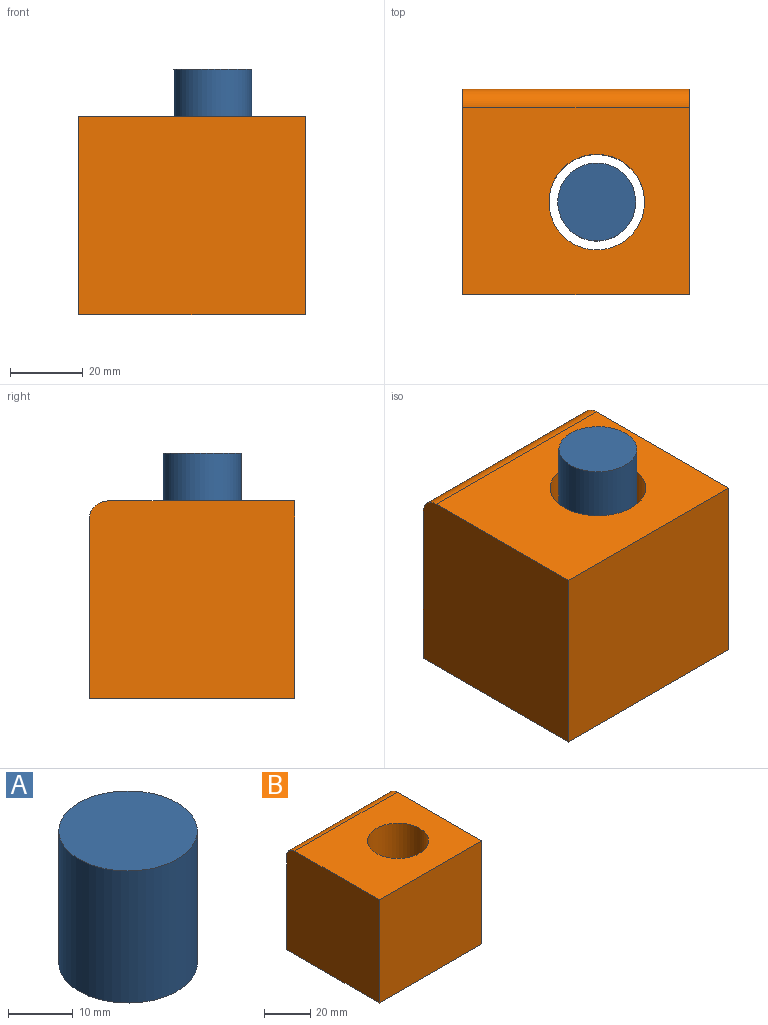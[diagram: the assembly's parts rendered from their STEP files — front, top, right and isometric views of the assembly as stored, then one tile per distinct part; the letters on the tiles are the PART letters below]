
ASSEMBLY  parts=2 mates=1
PART A: 3 faces, bbox 21.4x21.4x25 mm
  f0: cylinder r=10.71mm len=25mm, axis (0,0,-1), area 1682.9mm2, adj f1,f2
  f1: plane 21.43x21.43mm, normal (0,0,1), area 360.6mm2, adj f0
  f2: plane 21.43x21.43mm, normal (0,0,-1), area 360.6mm2, adj f0
PART B: 8 faces, bbox 62.2x56.5x54.4 mm
  f0: plane 56.45x54.36mm, normal (-1,0,0), area 3062.9mm2, adj f1,f3,f4,f5,f7
  f1: plane 62.2x54.36mm, normal (0,-1,0), area 3380.9mm2, adj f0,f2,f4,f5
  f2: plane 56.45x54.36mm, normal (1,0,0), area 3062.9mm2, adj f1,f3,f4,f5,f7
  f3: plane 62.2x49.28mm, normal (0,1,0), area 3064.9mm2, adj f0,f2,f5,f7
  f4: plane 62.2x51.37mm, normal (0,0,1), area 2652.7mm2, adj f0,f1,f2,f6,f7
  f5: plane 62.2x56.45mm, normal (0,0,-1), area 2968.7mm2, adj f0,f1,f2,f3,f6
  f6: cylinder r=13.14mm len=54.36mm, axis (0,0,1), area 4488mm2, adj f4,f5
  f7: cylinder r=5.08mm len=62.2mm, axis (1,0,0), area 496.3mm2, adj f0,f2,f3,f4
PLACE A t=(36.8,25.4,42.46)mm
PLACE B at identity
MATE slider A.f0 <-> B.f6  axis (0,0,-1) through (36.8,25.4,54.96)mm
